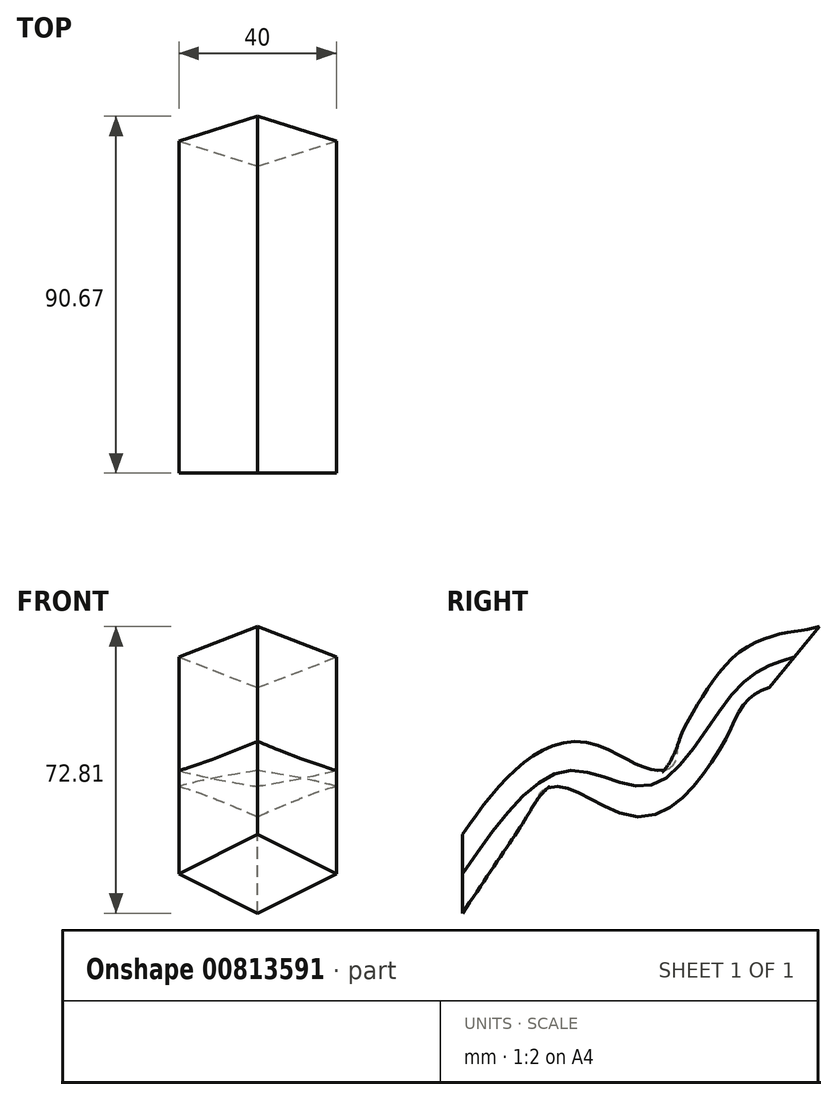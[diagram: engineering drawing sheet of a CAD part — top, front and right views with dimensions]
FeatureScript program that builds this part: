
annotation { "Feature Type Name" : "Feature", "Feature Type Description" : "" }
export const myFeature = defineFeature(function(context is Context, id is Id, definition is map)
    precondition{}
    {
        {
            var Q0;
            Q0=qCreatedBy(makeId("Front.planeOp"),FACE);
            var sketch = newSketch(context, id + "F0", { "sketchPlane" : qUnion([Q0])});
            skPoint(sketch, "E0.middle", {"position": v(0, 0) * mm});
            skLineSegment(sketch, "E1", {"start": v(0, 10) * mm, "end": v(-20, 0) * mm});
            skLineSegment(sketch, "E2", {"start": v(-20, 0) * mm, "end": v(0, -10) * mm});
            skLineSegment(sketch, "E3", {"start": v(0, -10) * mm, "end": v(20, 0) * mm});
            skLineSegment(sketch, "E4", {"start": v(20, 0) * mm, "end": v(0, 10) * mm});
            skPoint(sketch, "E5.orphan", {"position": v(-20, 10) * mm});
            skPoint(sketch, "E6.orphan", {"position": v(-20, -10) * mm});
            skPoint(sketch, "E7.orphan", {"position": v(20, -10) * mm});
            skPoint(sketch, "E0.top.start.orphan", {"position": v(20, 10) * mm});
            skSolve(sketch);
        }
        {
            var Q0;
            Q0=qCreatedBy(makeId("Right.planeOp"),FACE);
            var sketch = newSketch(context, id + "F1", { "sketchPlane" : qUnion([Q0])});
            skFitSpline(sketch, "E8", {"points": [v(0, 0) * mm, v(26.96, 26.22) * mm, v(48.31, 22.63) * mm, v(69.8, 47.05) * mm, v(84.35, 55.07) * mm], "startDerivative": vector(88.08, 127.69) * mm, "endDerivative": vector(73.63, 21.32) * mm});
            skSolve(sketch);
        }
        {
            var Q0;
            Q0 = qSketchRegion(id + "F0", true);
            var Q1;
            Q1 = qConstructionFilter(qBodyType(qCreatedBy(id + "F1" ,EDGE), BodyType.WIRE), ConstructionObject.NO);
            sweep(context, id + "F2", {"profiles" : qUnion([Q0]), "path" : qUnion([Q1])});
        }
    });
